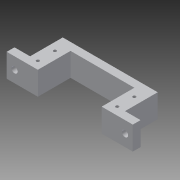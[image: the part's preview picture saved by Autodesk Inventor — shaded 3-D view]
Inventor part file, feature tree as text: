
AUTODESK INVENTOR PART (.ipt)
format: ipt  version: 2013 (Build 170138000, 138)  size: 105,984 bytes
history: native  units: mm
features: extrude x2, sketch x2, mirror x1
ambient origin geometry x8: Origin, YZ Plane, XZ Plane, XY Plane, X Axis, Y Axis, Z Axis, Center Point
bodies: Solid1 (feature_tree)
feature tree (5):
  extrude  "Extrusion1"  Depth=21.0mm
  extrude  "Extrusion2"  Depth=2.0mm
  mirror  "Mirror1"
  sketch  "Sketch1"  dims[d0=41.0mm d1=21.0mm]
  sketch  "Sketch2"  dims[d2=2.0mm d3=2.0mm d4=10.0mm d5=10.0mm d6=5.0mm d7=10.0mm d8=5.0mm d9=10.0mm d10=15.0mm d11=0.0mm d12=4.0mm d13=15.0mm d14=0.0mm]
